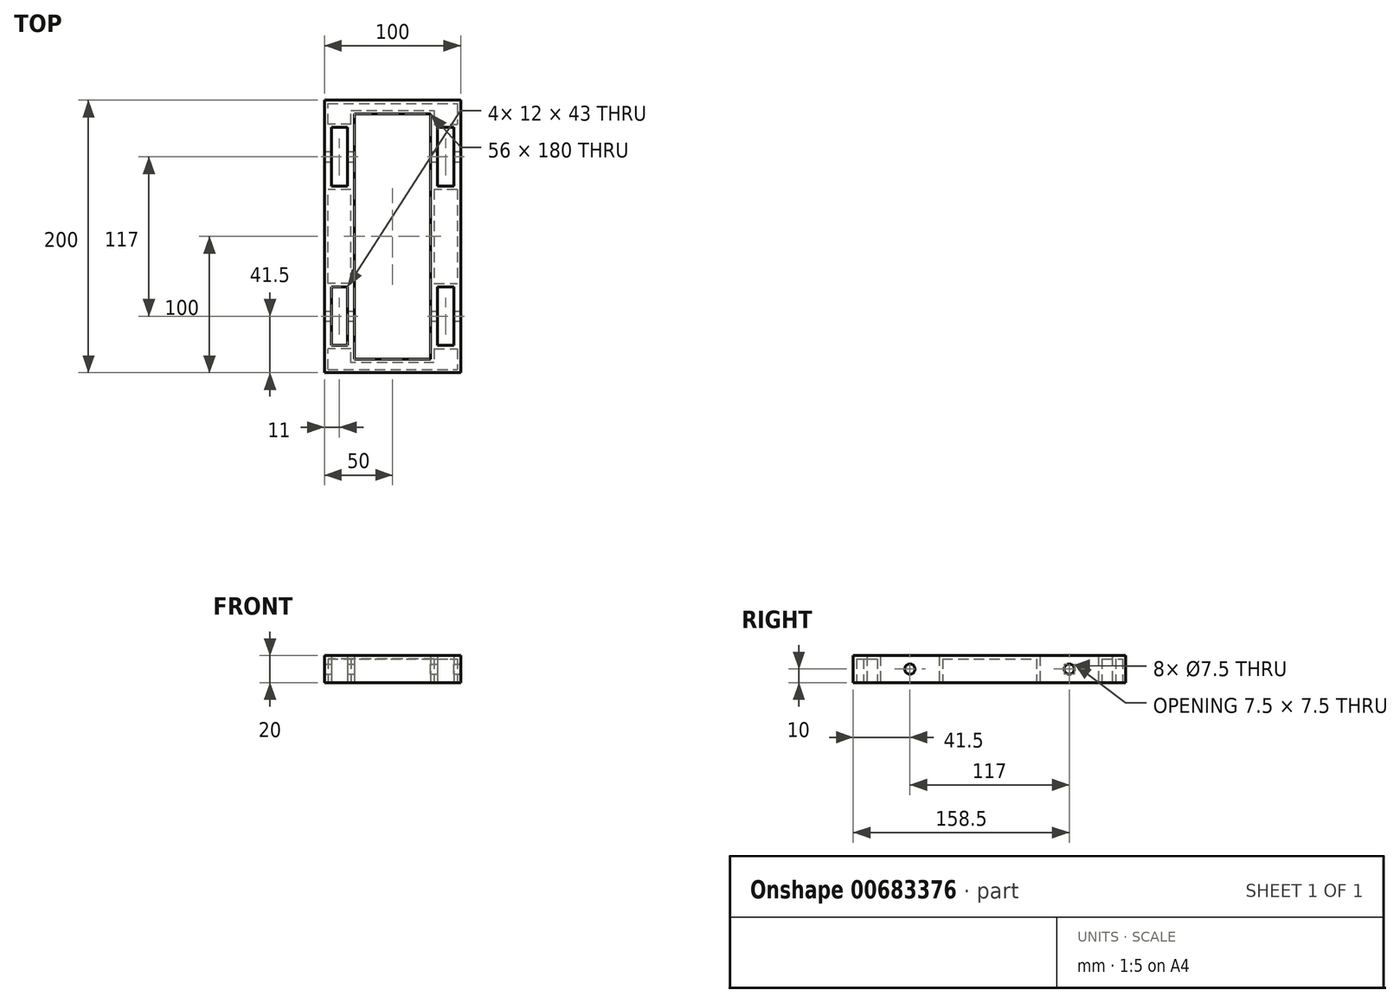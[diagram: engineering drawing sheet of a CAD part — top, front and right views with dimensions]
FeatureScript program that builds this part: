
annotation { "Feature Type Name" : "Feature", "Feature Type Description" : "" }
export const myFeature = defineFeature(function(context is Context, id is Id, definition is map)
    precondition{}
    {
        {
            var Q0;
            Q0=qCreatedBy(makeId("Top.planeOp"),FACE);
            var sketch = newSketch(context, id + "F0", { "sketchPlane" : qUnion([Q0])});
            skLineSegment(sketch, "E0", {"start": v(0, 0) * mm, "end": v(0, 200) * mm});
            skLineSegment(sketch, "E1", {"start": v(0, 0) * mm, "end": v(100, 0) * mm});
            skLineSegment(sketch, "E2", {"start": v(0, 200) * mm, "end": v(100, 200) * mm});
            skLineSegment(sketch, "E3", {"start": v(100, 200) * mm, "end": v(100, 0) * mm});
            skLineSegment(sketch, "E4", {"start": v(50, 200) * mm, "end": v(50, 190) * mm, "construction": true});
            skLineSegment(sketch, "E5", {"start": v(0, 100) * mm, "end": v(22, 100) * mm, "construction": true});
            skLineSegment(sketch, "E6", {"start": v(100, 100) * mm, "end": v(78, 100) * mm, "construction": true});
            skLineSegment(sketch, "E7", {"start": v(50, 0) * mm, "end": v(50, 10) * mm, "construction": true});
            skLineSegment(sketch, "E8", {"start": v(22, 190) * mm, "end": v(78, 190) * mm});
            skLineSegment(sketch, "E9", {"start": v(78, 190) * mm, "end": v(78, 10) * mm});
            skLineSegment(sketch, "E10", {"start": v(78, 10) * mm, "end": v(22, 10) * mm});
            skLineSegment(sketch, "E11", {"start": v(22, 10) * mm, "end": v(22, 190) * mm});
            skLineSegment(sketch, "E12", {"start": v(0, 10) * mm, "end": v(22, 10) * mm, "construction": true});
            skLineSegment(sketch, "E13", {"start": v(22, 190) * mm, "end": v(0, 190) * mm, "construction": true});
            skLineSegment(sketch, "E14", {"start": v(78, 190) * mm, "end": v(100, 190) * mm, "construction": true});
            skLineSegment(sketch, "E15", {"start": v(78, 10) * mm, "end": v(100, 10) * mm, "construction": true});
            skLineSegment(sketch, "E16", {"start": v(11, 10) * mm, "end": v(11, 20) * mm, "construction": true});
            skLineSegment(sketch, "E17", {"start": v(17, 20) * mm, "end": v(5, 20) * mm});
            skLineSegment(sketch, "E18", {"start": v(5, 20) * mm, "end": v(5, 63) * mm});
            skLineSegment(sketch, "E19", {"start": v(17, 20) * mm, "end": v(17, 63) * mm});
            skLineSegment(sketch, "E20", {"start": v(17, 63) * mm, "end": v(5, 63) * mm});
            skLineSegment(sketch, "E21", {"start": v(89, 10) * mm, "end": v(89, 20) * mm});
            skLineSegment(sketch, "E22", {"start": v(83, 20) * mm, "end": v(95, 20) * mm});
            skLineSegment(sketch, "E23", {"start": v(83, 63) * mm, "end": v(95, 63) * mm});
            skLineSegment(sketch, "E24", {"start": v(95, 63) * mm, "end": v(95, 20) * mm});
            skLineSegment(sketch, "E25", {"start": v(83, 20) * mm, "end": v(83, 63) * mm});
            skLineSegment(sketch, "E26", {"start": v(11, 190) * mm, "end": v(11, 180) * mm, "construction": true});
            skLineSegment(sketch, "E27", {"start": v(17, 180) * mm, "end": v(5, 180) * mm});
            skLineSegment(sketch, "E28", {"start": v(5, 180) * mm, "end": v(5, 137) * mm});
            skLineSegment(sketch, "E29", {"start": v(17, 180) * mm, "end": v(17, 137) * mm});
            skLineSegment(sketch, "E30", {"start": v(17, 137) * mm, "end": v(5, 137) * mm});
            skLineSegment(sketch, "E31", {"start": v(89, 190) * mm, "end": v(89, 180) * mm, "construction": true});
            skLineSegment(sketch, "E32", {"start": v(83, 180) * mm, "end": v(95, 180) * mm});
            skLineSegment(sketch, "E33", {"start": v(95, 180) * mm, "end": v(95, 137) * mm});
            skLineSegment(sketch, "E34", {"start": v(95, 137) * mm, "end": v(83, 137) * mm});
            skLineSegment(sketch, "E35", {"start": v(83, 137) * mm, "end": v(83, 180) * mm});
            skSolve(sketch);
        }
        {
            var Q0;
            Q0=makeQuery(id+"F0.imprint","IMPRINT",FACE,{"disambiguationData":[TD([[makeQuery(id+"F0.imprint","IMPRINT",EDGE,{"derivedFrom":sQuery(id+"F0.wireOp",EDGE,"E0")}),-1.0]])]});
            extrude(context, id + "F1", {"entities" : qUnion([Q0]), "depth" : 20 * mm, "offsetDistance" : 25 * mm});
        }
        {
            var Q0;
            Q0=makeQuery(id+"F1.opExtrude","SWEPT_FACE",FACE,{"disambiguationData":[OSD([sQuery(id+"F0.wireOp",EDGE,"E3")])]});
            var sketch = newSketch(context, id + "F2", { "sketchPlane" : qUnion([Q0])});
            skPoint(sketch, "E36.0", {"position": v(41.5, 20) * mm});
            skPoint(sketch, "E37.0", {"position": v(41.5, 0) * mm});
            skPoint(sketch, "E38.0", {"position": v(158.5, 20) * mm});
            skPoint(sketch, "E39.0", {"position": v(158.5, 0) * mm});
            skLineSegment(sketch, "E40", {"start": v(41.5, 20) * mm, "end": v(41.5, 0) * mm, "construction": true});
            skLineSegment(sketch, "E41", {"start": v(158.5, 20) * mm, "end": v(158.5, 0) * mm, "construction": true});
            skCircle(sketch, "E42", {"center": v(41.5, 10) * mm, "radius": 3.75 * mm});
            skCircle(sketch, "E43", {"center": v(158.5, 10) * mm, "radius": 3.75 * mm});
            skSolve(sketch);
        }
        {
            var Q0;
            Q0=makeQuery(id+"F2.imprint","IMPRINT",FACE,{"disambiguationData":[TD([[makeQuery(id+"F2.imprint","IMPRINT",EDGE,{"derivedFrom":sQuery(id+"F2.wireOp",EDGE,"E42")}),1.0]])]});
            var Q1;
            Q1=makeQuery(id+"F2.imprint","IMPRINT",FACE,{"disambiguationData":[TD([[makeQuery(id+"F2.imprint","IMPRINT",EDGE,{"derivedFrom":sQuery(id+"F2.wireOp",EDGE,"E43")}),1.0]])]});
            extrude(context, id + "F3", {"entities" : qUnion([Q0, Q1]), "operationType" : NewBodyOperationType.REMOVE, "endBound" : BoundingType.THROUGH_ALL, "oppositeDirection" : true, "depth" : 25 * mm, "offsetDistance" : 25 * mm});
        }
        {
            var Q0;
            Q0=makeQuery(id+"F1.opExtrude","CAP_FACE",FACE,{"disambiguationData":[OSD([sQuery(id+"F0.wireOp",EDGE,"E0"),sQuery(id+"F0.wireOp",EDGE,"E1"),sQuery(id+"F0.wireOp",EDGE,"E2"),sQuery(id+"F0.wireOp",EDGE,"E3"),sQuery(id+"F0.wireOp",EDGE,"E8"),sQuery(id+"F0.wireOp",EDGE,"E9"),sQuery(id+"F0.wireOp",EDGE,"E10"),sQuery(id+"F0.wireOp",EDGE,"E11"),sQuery(id+"F0.wireOp",EDGE,"E17"),sQuery(id+"F0.wireOp",EDGE,"E18"),sQuery(id+"F0.wireOp",EDGE,"E19"),sQuery(id+"F0.wireOp",EDGE,"E20"),sQuery(id+"F0.wireOp",EDGE,"E22"),sQuery(id+"F0.wireOp",EDGE,"E23"),sQuery(id+"F0.wireOp",EDGE,"E24"),sQuery(id+"F0.wireOp",EDGE,"E25"),sQuery(id+"F0.wireOp",EDGE,"E27"),sQuery(id+"F0.wireOp",EDGE,"E28"),sQuery(id+"F0.wireOp",EDGE,"E29"),sQuery(id+"F0.wireOp",EDGE,"E30"),sQuery(id+"F0.wireOp",EDGE,"E32"),sQuery(id+"F0.wireOp",EDGE,"E33"),sQuery(id+"F0.wireOp",EDGE,"E34"),sQuery(id+"F0.wireOp",EDGE,"E35")])],"isStart":true});
            shell(context, id + "F4", {"entities" : qUnion([Q0]), "thickness" : 2.5 * mm});
        }
    });
